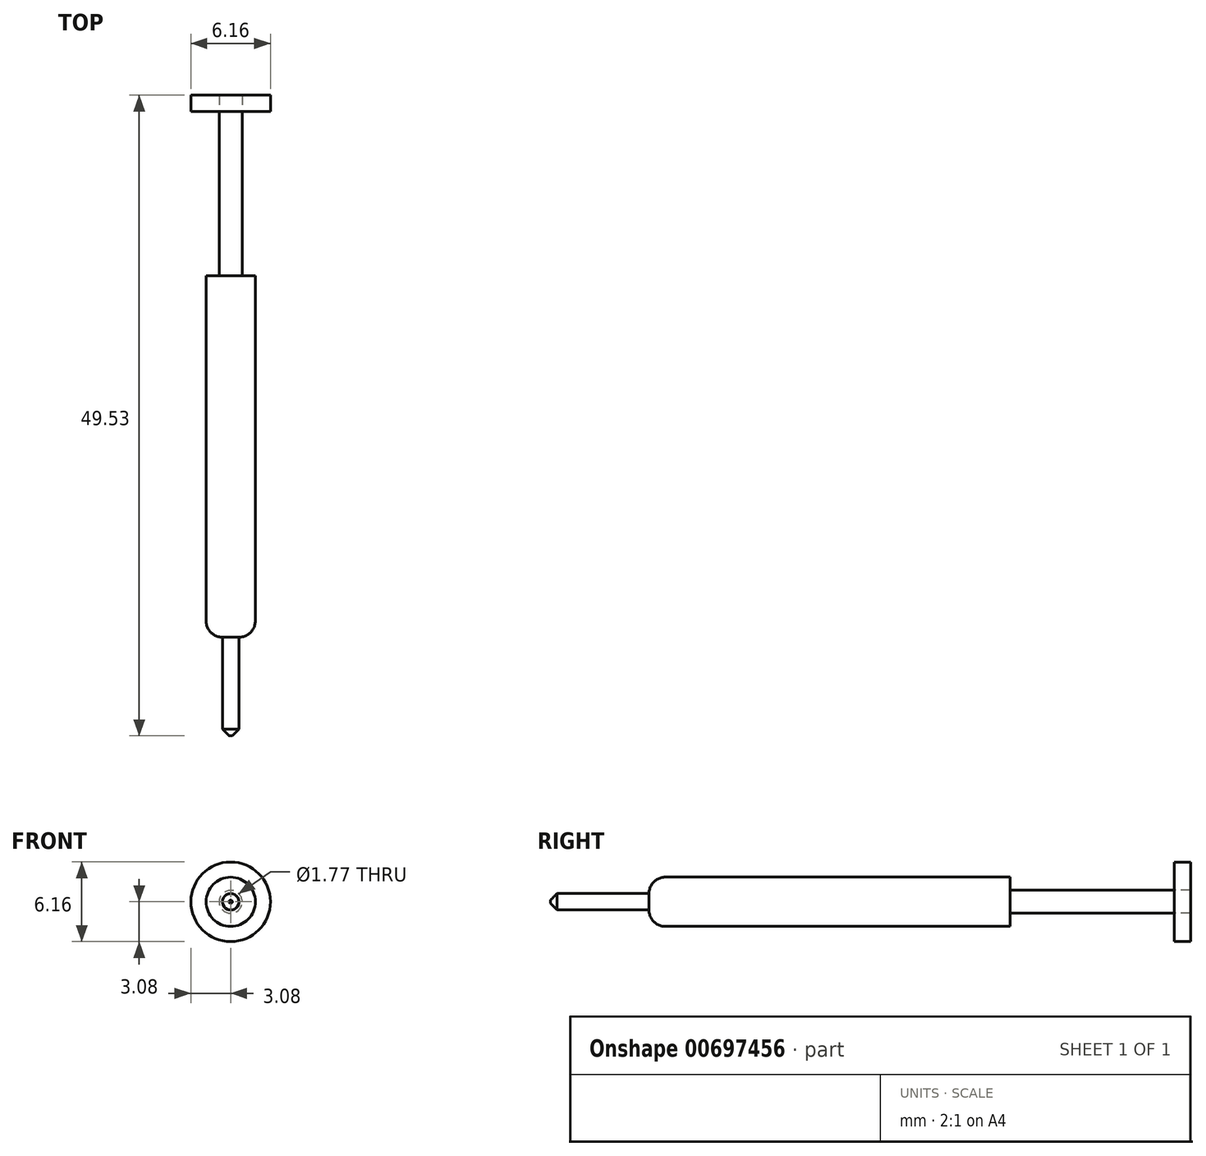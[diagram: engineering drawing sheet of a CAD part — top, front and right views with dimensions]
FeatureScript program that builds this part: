
annotation { "Feature Type Name" : "Feature", "Feature Type Description" : "" }
export const myFeature = defineFeature(function(context is Context, id is Id, definition is map)
    precondition{}
    {
        {
            var Q0;
            Q0=qCreatedBy(makeId("Front.planeOp"),FACE);
            var sketch = newSketch(context, id + "F0", { "sketchPlane" : qUnion([Q0])});
            skCircle(sketch, "E0", {"center": v(0, 0) * mm, "radius": 1.9 * mm});
            skSolve(sketch);
        }
        {
            var Q0;
            Q0=makeQuery(id+"F0.imprint","IMPRINT",FACE,{"disambiguationData":[TD([[makeQuery(id+"F0.imprint","IMPRINT",EDGE,{"derivedFrom":sQuery(id+"F0.wireOp",EDGE,"E0")}),1.0]])]});
            extrude(context, id + "F1", {"entities" : qUnion([Q0]), "depth" : 27.94 * mm, "offsetDistance" : 25.4 * mm});
        }
        {
            var Q0;
            Q0=makeQuery(id+"F1.opExtrude","CAP_EDGE",EDGE,{"disambiguationData":[OSD([sQuery(id+"F0.wireOp",EDGE,"E0")])],"isStart":false});
            fillet(context, id + "F2", {"entities" : qUnion([Q0]), "radius" : 1.27 * mm, "tangentPropagation" : true, "allowEdgeOverflow" : false});
        }
        {
            var Q0;
            Q0=makeQuery(id+"F1.opExtrude","CAP_FACE",FACE,{"disambiguationData":[OSD([sQuery(id+"F0.wireOp",EDGE,"E0")])],"isStart":false});
            extrude(context, id + "F3", {"entities" : qUnion([Q0]), "operationType" : NewBodyOperationType.ADD, "depth" : 7.62 * mm, "offsetDistance" : 25.4 * mm});
        }
        {
            var Q0;
            Q0=makeQuery(id+"F3.opExtrude","CAP_EDGE",EDGE,{"disambiguationData":[OSD([sQuery(id+"F0.wireOp",EDGE,"E0")])],"isStart":false});
            fillet(context, id + "F4", {"entities" : qUnion([Q0]), "radius" : 0.5 * mm, "tangentPropagation" : true, "rho" : 0, "crossSection" : FilletCrossSection.CONIC, "allowEdgeOverflow" : false});
        }
        {
            var Q0;
            Q0=makeQuery(id+"F1.opExtrude","CAP_FACE",FACE,{"disambiguationData":[OSD([sQuery(id+"F0.wireOp",EDGE,"E0")])],"isStart":true});
            var sketch = newSketch(context, id + "F5", { "sketchPlane" : qUnion([Q0])});
            skCircle(sketch, "E1", {"center": v(0, 0) * mm, "radius": 0.89 * mm});
            skSolve(sketch);
        }
        {
            var Q0;
            Q0=makeQuery(id+"F5.imprint","IMPRINT",FACE,{"disambiguationData":[TD([[makeQuery(id+"F5.imprint","IMPRINT",EDGE,{"derivedFrom":sQuery(id+"F5.wireOp",EDGE,"E1")}),1.0]])]});
            extrude(context, id + "F6", {"entities" : qUnion([Q0]), "operationType" : NewBodyOperationType.ADD, "depth" : 12.7 * mm, "offsetDistance" : 25.4 * mm});
        }
        {
            var Q0;
            Q0=makeQuery(id+"F6.opExtrude","CAP_FACE",FACE,{"disambiguationData":[OSD([sQuery(id+"F5.wireOp",EDGE,"E1")])],"isStart":false});
            var sketch = newSketch(context, id + "F7", { "sketchPlane" : qUnion([Q0])});
            skCircle(sketch, "E2", {"center": v(0, 0) * mm, "radius": 3.08 * mm});
            skSolve(sketch);
        }
        {
            var Q0;
            Q0=makeQuery(id+"F7.imprint","IMPRINT",FACE,{"disambiguationData":[TD([[makeQuery(id+"F7.imprint","IMPRINT",EDGE,{"derivedFrom":sQuery(id+"F7.wireOp",EDGE,"E2")}),1.0]])]});
            extrude(context, id + "F8", {"entities" : qUnion([Q0]), "depth" : 1.27 * mm, "offsetDistance" : 25.4 * mm});
        }
    });
